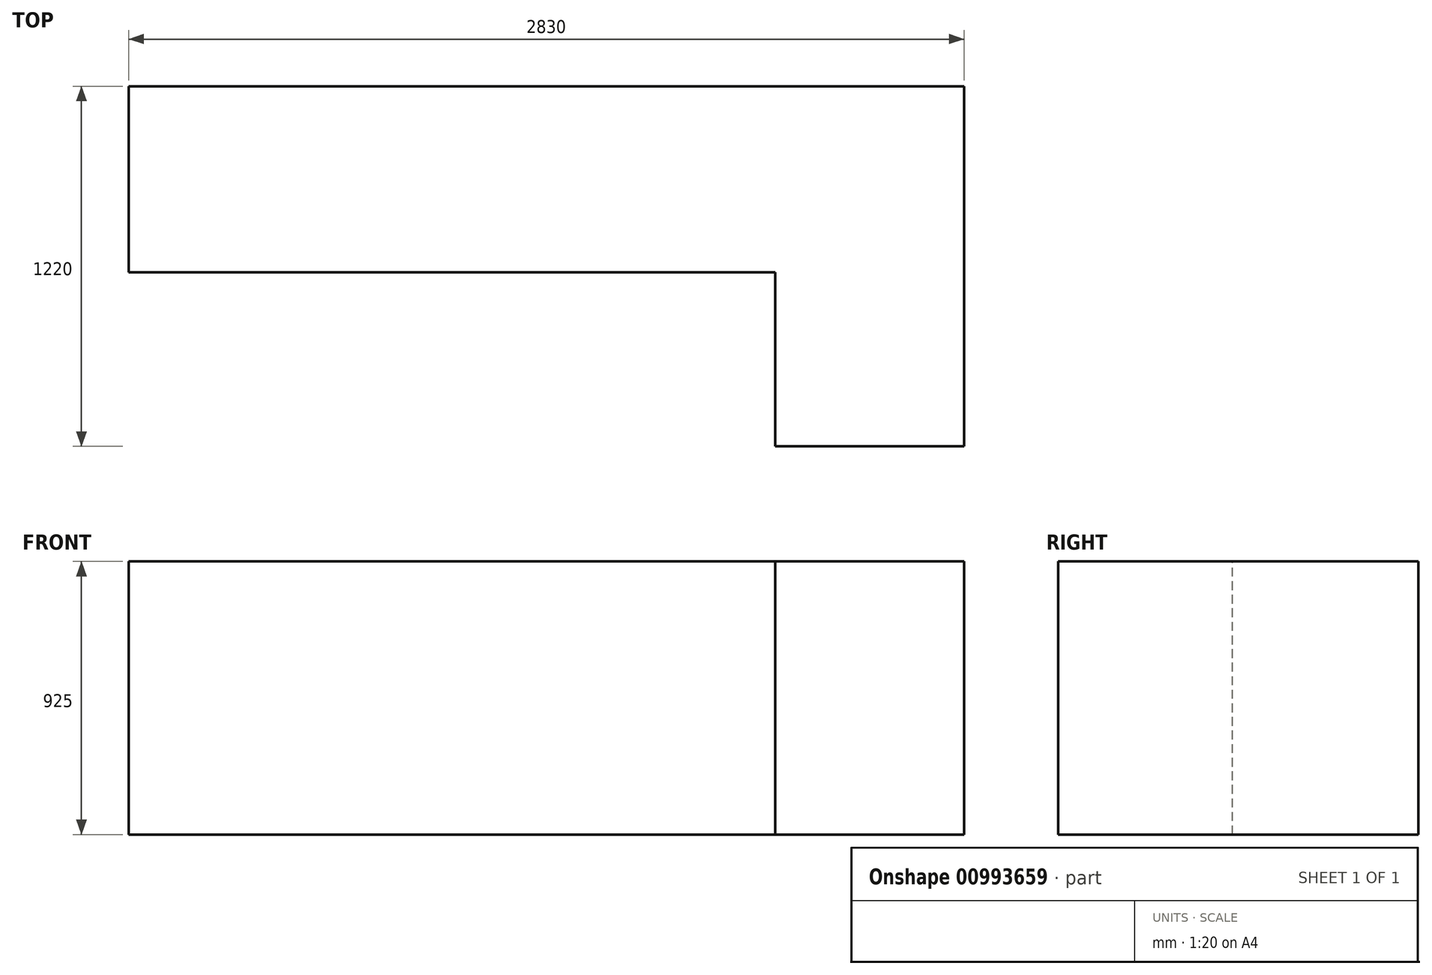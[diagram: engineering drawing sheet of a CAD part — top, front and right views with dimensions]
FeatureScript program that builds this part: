
annotation { "Feature Type Name" : "Feature", "Feature Type Description" : "" }
export const myFeature = defineFeature(function(context is Context, id is Id, definition is map)
    precondition{}
    {
        {
            var Q0;
            Q0=qCreatedBy(makeId("Top.planeOp"),FACE);
            var sketch = newSketch(context, id + "F0", { "sketchPlane" : qUnion([Q0])});
            skLineSegment(sketch, "E0", {"start": v(-1095, 315) * mm, "end": v(-1095, -315) * mm});
            skLineSegment(sketch, "E1", {"start": v(-1095, -315) * mm, "end": v(1095, -315) * mm});
            skLineSegment(sketch, "E2", {"start": v(1095, -315) * mm, "end": v(1095, -905) * mm});
            skLineSegment(sketch, "E3", {"start": v(1095, -905) * mm, "end": v(1735, -905) * mm});
            skLineSegment(sketch, "E4", {"start": v(1735, -905) * mm, "end": v(1735, 315) * mm});
            skLineSegment(sketch, "E5", {"start": v(1735, 315) * mm, "end": v(-1095, 315) * mm});
            skLineSegment(sketch, "E6", {"start": v(-109.22, 0) * mm, "end": v(200.11, 0) * mm, "construction": true});
            skLineSegment(sketch, "E7", {"start": v(0, 137.62) * mm, "end": v(0, -181.48) * mm, "construction": true});
            skSolve(sketch);
        }
        {
            var Q0;
            Q0 = qSketchRegion(id + "F0", true);
            extrude(context, id + "F1", {"entities" : qUnion([Q0]), "oppositeDirection" : true, "depth" : 925 * mm, "offsetDistance" : 25.4 * mm});
        }
    });
